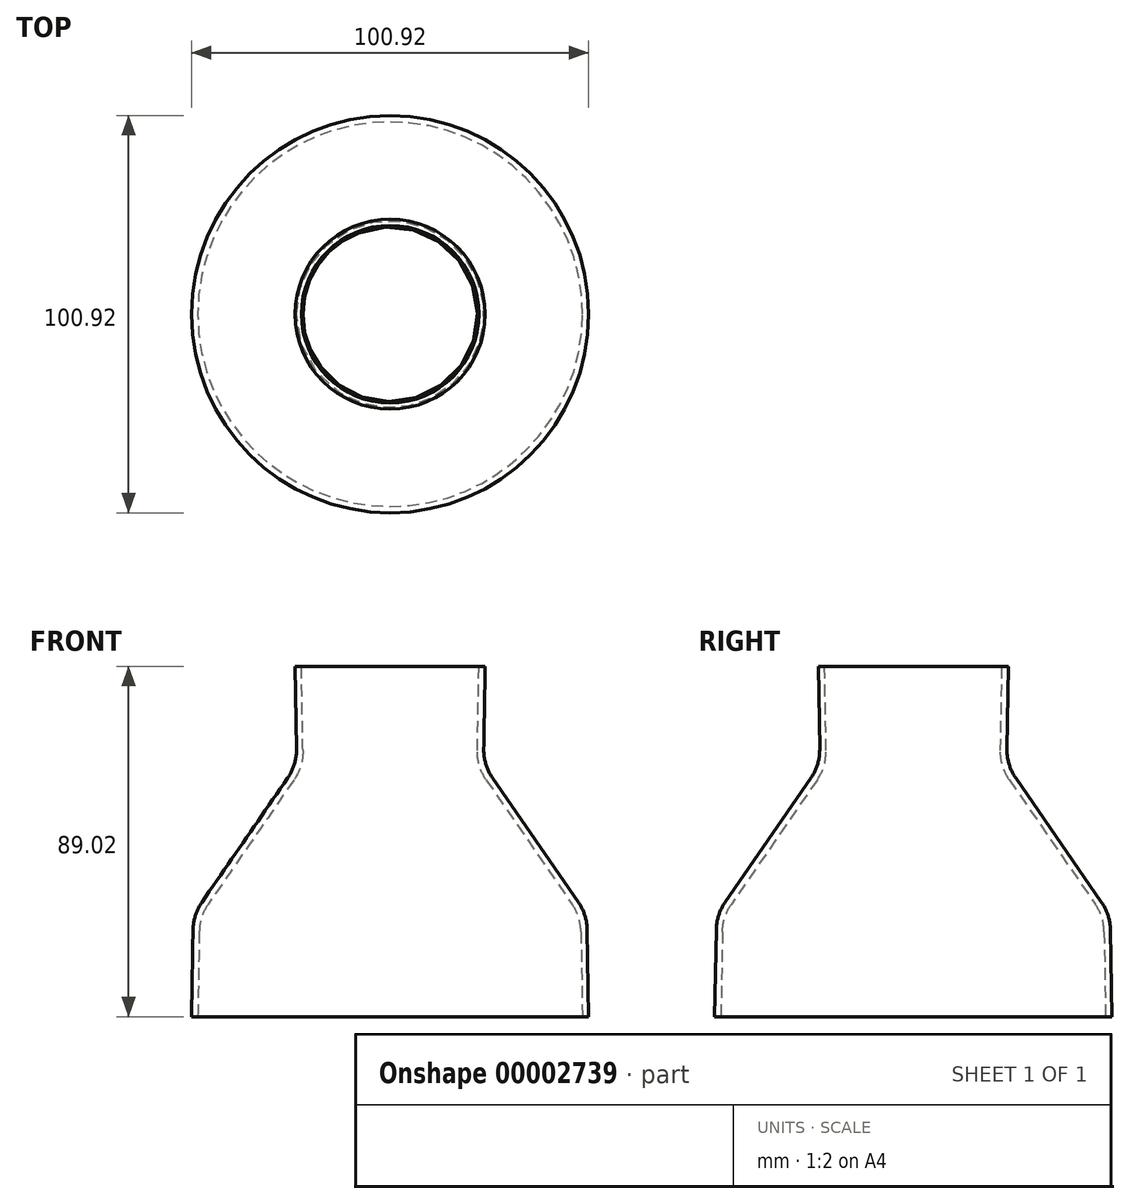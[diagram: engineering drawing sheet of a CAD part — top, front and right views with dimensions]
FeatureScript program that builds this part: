
annotation { "Feature Type Name" : "Feature", "Feature Type Description" : "" }
export const myFeature = defineFeature(function(context is Context, id is Id, definition is map)
    precondition{}
    {
        {
            var Q0;
            Q0=qCreatedBy(makeId("Front.planeOp"),FACE);
            var sketch = newSketch(context, id + "F0", { "sketchPlane" : qUnion([Q0])});
            skLineSegment(sketch, "E0", {"start": v(48.86, 0) * mm, "end": v(48.41, 25.4) * mm});
            skLineSegment(sketch, "E1", {"start": v(48.41, 25.4) * mm, "end": v(22.1, 63.5) * mm});
            skLineSegment(sketch, "E2", {"start": v(22.1, 63.5) * mm, "end": v(22.54, 88.9) * mm});
            skLineSegment(sketch, "E3", {"start": v(0, 0) * mm, "end": v(0, 58.65) * mm});
            skLineSegment(sketch, "E4", {"start": v(22.54, 88.9) * mm, "end": v(24.15, 89.02) * mm});
            skLineSegment(sketch, "E5", {"start": v(24.15, 89.02) * mm, "end": v(23.7, 63.99) * mm});
            skLineSegment(sketch, "E6", {"start": v(23.7, 63.99) * mm, "end": v(50, 25.91) * mm});
            skLineSegment(sketch, "E7", {"start": v(50, 25.91) * mm, "end": v(50.46, 0) * mm});
            skLineSegment(sketch, "E8", {"start": v(50.46, 0) * mm, "end": v(48.86, 0) * mm});
            skSolve(sketch);
        }
        {
            var Q0;
            Q0=makeQuery(id+"F0.imprint","IMPRINT",FACE,{"disambiguationData":[TD([[makeQuery(id+"F0.imprint","IMPRINT",EDGE,{"derivedFrom":sQuery(id+"F0.wireOp",EDGE,"E0")}),-1.0]])]});
            var Q1;
            Q1=sQuery(id+"F0.wireOp",EDGE,"E1");
            var Q2;
            Q2=sQuery(id+"F0.wireOp",EDGE,"E6");
            var Q3;
            Q3=sQuery(id+"F0.wireOp",EDGE,"E7");
            var Q4;
            Q4=sQuery(id+"F0.wireOp",EDGE,"E5");
            var Q5;
            Q5=sQuery(id+"F0.wireOp",EDGE,"E0");
            var Q6;
            Q6=sQuery(id+"F0.wireOp",EDGE,"E2");
            var Q7;
            Q7=sQuery(id+"F0.wireOp",EDGE,"E4");
            var Q8;
            Q8=sQuery(id+"F0.wireOp",EDGE,"E8");
            var Q9;
            Q9=sQuery(id+"F0.wireOp",EDGE,"E3");
            revolve(context, id + "F1", {"entities" : qUnion([Q0]), "surfaceEntities" : qUnion([Q1, Q2, Q3, Q4, Q5, Q6, Q7, Q8]), "axis" : qUnion([Q9]), "revolveType" : RevolveType.FULL});
        }
        {
            var Q0;
            Q0=makeQuery(id+"F1.opRevolve","SWEPT_EDGE",EDGE,{"disambiguationData":[OSD([sQuery(id+"F0.wireOp",EDGE,"E6"),sQuery(id+"F0.wireOp",EDGE,"E7")])]});
            var Q1;
            Q1=makeQuery(id+"F1.opRevolve","SWEPT_EDGE",EDGE,{"disambiguationData":[OSD([sQuery(id+"F0.wireOp",EDGE,"E5"),sQuery(id+"F0.wireOp",EDGE,"E6")])]});
            var Q2;
            Q2=makeQuery(id+"F1.opRevolve","SWEPT_EDGE",EDGE,{"disambiguationData":[OSD([sQuery(id+"F0.wireOp",EDGE,"E1"),sQuery(id+"F0.wireOp",EDGE,"E2")])]});
            var Q3;
            Q3=makeQuery(id+"F1.opRevolve","SWEPT_EDGE",EDGE,{"disambiguationData":[OSD([sQuery(id+"F0.wireOp",EDGE,"E0"),sQuery(id+"F0.wireOp",EDGE,"E1")])]});
            fillet(context, id + "F2", {"entities" : qUnion([Q0, Q1, Q2, Q3]), "radius" : 12.7 * mm, "tangentPropagation" : true, "allowEdgeOverflow" : false});
        }
    });
